# Revit family: QF_COMENDA_6F030X_DDPS_DR_DRDDPS_CAT
name_source: partatom
category: Attrezzature speciali
units: mm (PartAtom-declared; Revit-internal decimal feet)

## family parameters
Basato su piano di lavoro = No
Condiviso = No
Numero OmniClass = 23.40.40.14
Punto di calcolo locali = No
Quota connettore circolare = Usa diametro
Sempre verticale = Sì
Taglio con vuoti quando caricato = No
Tipo di parte = Normale
Titolo OmniClass = Food Service Equipment

## types (15) — shared parameters
Altezza = 820 mm  [stored 2.69029 ft]
Altezza allacciamento elettrico da pavimento finito = 55 mm  [stored 0.180446 ft]
Altezza da terra raccordo acqua calda = 55 mm  [stored 0.180446 ft]
Altezza dello scarico diretto acqua da pavimento finito = 55 mm  [stored 0.180446 ft]
Base stand with door = No
Corrente di funzionamento normale = 11 A
Diametro dello scarico diretto di acqua = 1 1/2"
Diametro raccordo acqua calda = 1"
Fase = 3
Frequenza = 50 Hz
Lunghezza = 600 mm
Numero dei poli = 3
Peso netto = 58.00 kg
Potenza elettrica = 5450 W
Pressione minima acqua calda = 2000.0 Pa
Produttore = COMENDA
Profondità = 605 mm  [stored 1.98491 ft]
Protezione contro le sovracorrenti = 16 A
Stand feet kit = No
Temperatura raccomandata per acqua calda = 50 °C
Tensione = 400 V
URL = www.comenda.eu
zero-valued in all types: HEIGHT FROM THE FLOOR, Prospetto di default

## per-type parameters (varying)
| type | Descrizione | Modello | URL catalogo |
| 6F0300 | MULTIPOWER DISHWASHER | PF45 |  |
| 6F0301 | MULTIPOWER DISHWASHER WITH RCD | PF45 R |  |
| 6F0304 | MULTIPOWER DISHWASHER WITH RCD, WATER SOFTENER | PF45 RA |  |
| 6F0301DR | MULTIPOWER DOUBLE RACK DISHWASHER WITH RCD | PF45 R DR |  |
| 6F0304DR | MULTIPOWER DOUBLE RACK DISHWASHER WITH RCD AND WATER SOFTENER | PF45 RA DR |  |
| 6F0300DDPS | MULTIPOWER DISHWASHER WITH DRAIN PUMP, DETERGENT DOSING PUMP | PF45+ | https://comenda.eu |
| 6F0301DDPS | MULTIPOWER DISHWASHER WITH RCD, DRAIN PUMP, DETERGENT DOSING PUMP | PF45 R+ | https://comenda.eu |
| 6F0301DRDDPS | MULTIPOWER DOUBLE RACK DISHWASHER WITH RCD, DRAIN PUMP, DETERGENT DOSING PUMP | PF45 R DR+ | https://comenda.eu |
| 6F0304DDPS | MULTIPOWER DISHWASHER WITH RCD, WATER SOFTENER, DRAIN PUMP, DETERGENT DOSING PUMP | PF45 RA+ | https://comenda.eu |
| 6F0304DRDDPS | MULTIPOWER DOUBLE RACK DISHWASHER WITH RCD, WATER SOFTENER, DRAIN PUMP, DETERGENT DOSING PUMP | PF45 RA DR+ | https://comenda.eu |
| 6F0300DD | MULTIPOWER DISHWASHER, WITH DETERGENT DOSING PUMP | PF45 DD | https://comenda.eu |
| 6F0301DD | MULTIPOWER DISHWASHER WITH RCD AND DETERGENT DOSING PUMP | PF45 R DD | https://comenda.eu |
| 6F0304DD | MULTIPOWER DISHWASHER WITH RCD, WATER SOFTENER AND DETERGENT DOSING PUMP | PF45 RA DD | https://comenda.eu |
| 6F0301DRDD | MULTIPOWER DOUBLE RACK DISHWASHER WITH RCD AND | PF45 R DR DD | https://comenda.eu |
| 6F0304DRDD | MULTIPOWER DOUBLE RACK DISHWASHER WITH RCD, WATER SOFTENER AND DETERGENT DOSING PUMP | PF45 RA DR DD | https://comenda.eu |

note: [stored X ft] marks values corroborated as IEEE doubles in the binary element streams (Revit-internal decimal feet)

## geometry (parser evidence)
native form markers: Sweep x4
no freeform markers — native parametric forms only
